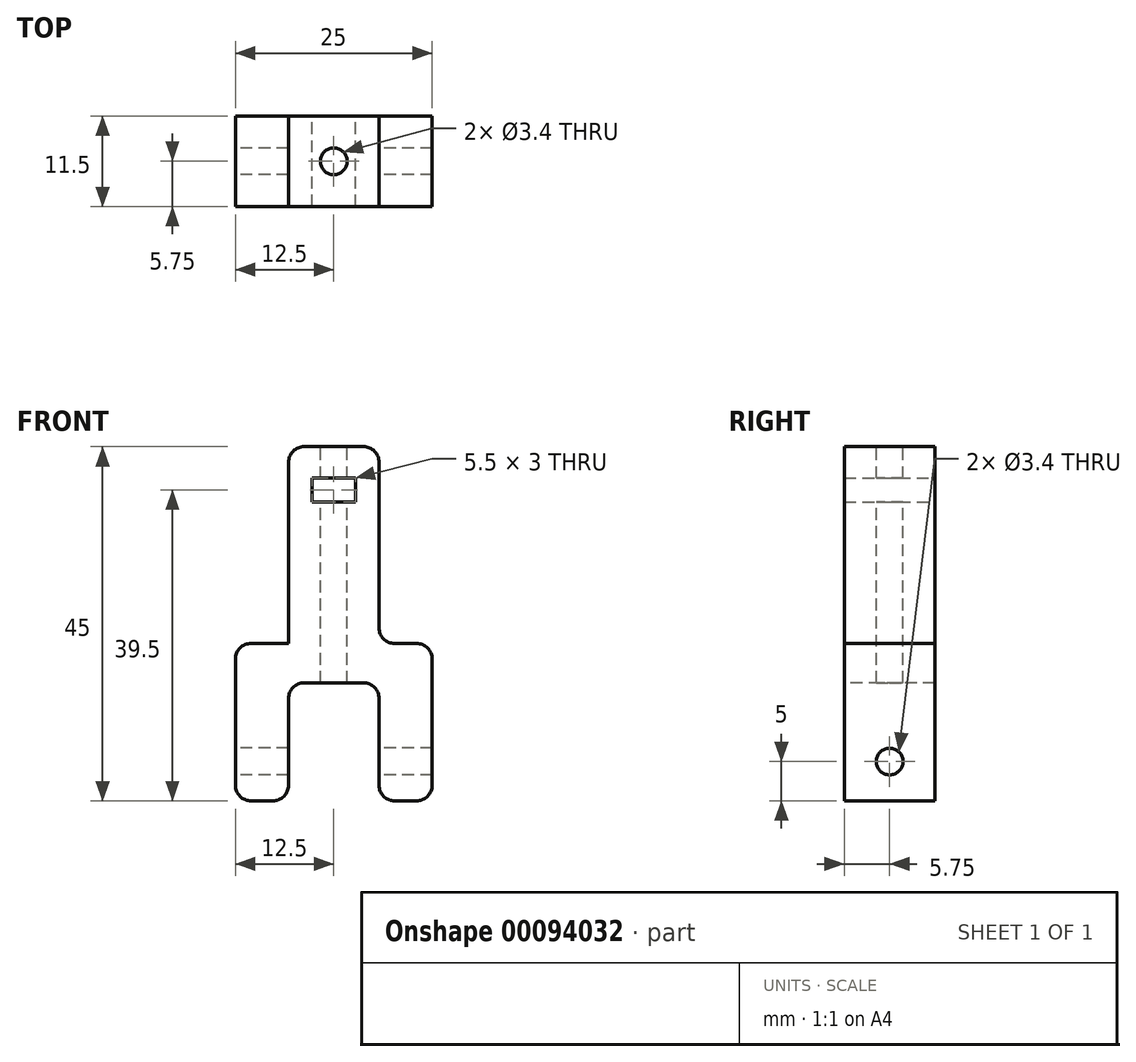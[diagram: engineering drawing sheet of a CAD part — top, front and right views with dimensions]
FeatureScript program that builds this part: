
annotation { "Feature Type Name" : "Feature", "Feature Type Description" : "" }
export const myFeature = defineFeature(function(context is Context, id is Id, definition is map)
    precondition{}
    {
        {
            var Q0;
            Q0=qCreatedBy(makeId("Top.planeOp"),FACE);
            var sketch = newSketch(context, id + "F0", { "sketchPlane" : qUnion([Q0])});
            skLineSegment(sketch, "E0.bottom", {"start": v(5.75, 5.75) * mm, "end": v(-5.75, 5.75) * mm});
            skLineSegment(sketch, "E0.top", {"start": v(5.75, -5.75) * mm, "end": v(-5.75, -5.75) * mm});
            skLineSegment(sketch, "E0.left", {"start": v(5.75, 5.75) * mm, "end": v(5.75, -5.75) * mm});
            skLineSegment(sketch, "E0.right", {"start": v(-5.75, 5.75) * mm, "end": v(-5.75, -5.75) * mm});
            skPoint(sketch, "E0.middle", {"position": v(0, 0) * mm});
            skLineSegment(sketch, "E1.bottom", {"start": v(12.5, 5.75) * mm, "end": v(-12.5, 5.75) * mm});
            skLineSegment(sketch, "E1.top", {"start": v(12.5, -5.75) * mm, "end": v(-12.5, -5.75) * mm});
            skLineSegment(sketch, "E1.left", {"start": v(12.5, 5.75) * mm, "end": v(12.5, -5.75) * mm});
            skLineSegment(sketch, "E1.right", {"start": v(-12.5, 5.75) * mm, "end": v(-12.5, -5.75) * mm});
            skSolve(sketch);
        }
        {
            var Q0;
            {var subQ0=sQuery(id+"F0.wireOp",EDGE,"E0.right");Q0=makeQuery(id+"F0.imprint","IMPRINT",FACE,{"disambiguationData":[TD([[makeQuery(id+"F0.imprint","IMPRINT",EDGE,{"derivedFrom":subQ0}),-1.0]])]});}
            var Q1;
            {var subQ0=sQuery(id+"F0.wireOp",EDGE,"E0.left");Q1=makeQuery(id+"F0.imprint","IMPRINT",FACE,{"disambiguationData":[TD([[makeQuery(id+"F0.imprint","IMPRINT",EDGE,{"derivedFrom":subQ0}),1.0]])]});}
            var Q2;
            {var subQ0=sQuery(id+"F0.wireOp",EDGE,"E0.left");Q2=makeQuery(id+"F0.imprint","IMPRINT",FACE,{"disambiguationData":[TD([[makeQuery(id+"F0.imprint","IMPRINT",EDGE,{"derivedFrom":subQ0}),-1.0]])]});}
            extrude(context, id + "F1", {"entities" : qUnion([Q0, Q1, Q2]), "oppositeDirection" : true, "depth" : 5 * mm});
        }
        {
            var Q0;
            {var subQ0=sQuery(id+"F0.wireOp",EDGE,"E0.left");Q0=makeQuery(id+"F0.imprint","IMPRINT",FACE,{"disambiguationData":[TD([[makeQuery(id+"F0.imprint","IMPRINT",EDGE,{"derivedFrom":subQ0}),1.0]])]});}
            var Q1;
            {var subQ0=sQuery(id+"F0.wireOp",EDGE,"E0.right");Q1=makeQuery(id+"F0.imprint","IMPRINT",FACE,{"disambiguationData":[TD([[makeQuery(id+"F0.imprint","IMPRINT",EDGE,{"derivedFrom":subQ0}),-1.0]])]});}
            extrude(context, id + "F2", {"entities" : qUnion([Q0, Q1]), "operationType" : NewBodyOperationType.ADD, "oppositeDirection" : true, "depth" : 20 * mm});
        }
        {
            var Q0;
            {var subQ0=sQuery(id+"F0.wireOp",EDGE,"E0.left");Q0=makeQuery(id+"F0.imprint","IMPRINT",FACE,{"disambiguationData":[TD([[makeQuery(id+"F0.imprint","IMPRINT",EDGE,{"derivedFrom":subQ0}),-1.0]])]});}
            extrude(context, id + "F3", {"entities" : qUnion([Q0]), "operationType" : NewBodyOperationType.ADD, "depth" : 25 * mm});
        }
        {
            var Q0;
            {var subQ0=sQuery(id+"F0.wireOp",EDGE,"E1.right");Q0=makeQuery(id+"F2.boolean.opBoolean","MERGE",FACE,{"derivedFrom":[makeQuery(id+"F1.opExtrude","SWEPT_FACE",FACE,{"disambiguationData":[OSD([subQ0])]}),makeQuery(id+"F2.opExtrude","SWEPT_FACE",FACE,{"disambiguationData":[OSD([subQ0])]})]});}
            var sketch = newSketch(context, id + "F4", { "sketchPlane" : qUnion([Q0])});
            skCircle(sketch, "E2", {"center": v(0, -15) * mm, "radius": 1.7 * mm});
            skSolve(sketch);
        }
        {
            var Q0;
            Q0 = qSketchRegion(id + "F4", true);
            extrude(context, id + "F5", {"entities" : qUnion([Q0]), "operationType" : NewBodyOperationType.REMOVE, "endBound" : BoundingType.THROUGH_ALL, "oppositeDirection" : true, "depth" : 25 * mm});
        }
        {
            var Q0;
            {var subQ0=sQuery(id+"F0.wireOp",EDGE,"E1.bottom");Q0=makeQuery(id+"F3.boolean.opBoolean","MERGE",FACE,{"derivedFrom":[makeQuery(id+"F2.boolean.opBoolean","MERGE",FACE,{"derivedFrom":[makeQuery(id+"F1.opExtrude","SWEPT_FACE",FACE,{"disambiguationData":[OSD([subQ0])]}),makeQuery(id+"F2.opExtrude","SWEPT_FACE",FACE,{"disambiguationData":[OSD([subQ0]),TDD([makeQuery(id+"F0.imprint","IMPRINT",EDGE,{"disambiguationData":[TD([[makeQuery(id+"F0.imprint","INTERSECT",VERTEX,{"derivedFrom":[sQuery(id+"F0.wireOp",EDGE,"E0.left"),subQ0]}),1.0]])],"derivedFrom":subQ0})])]}),makeQuery(id+"F2.opExtrude","SWEPT_FACE",FACE,{"disambiguationData":[OSD([subQ0]),TDD([makeQuery(id+"F0.imprint","IMPRINT",EDGE,{"disambiguationData":[TD([[makeQuery(id+"F0.imprint","INTERSECT",VERTEX,{"derivedFrom":[sQuery(id+"F0.wireOp",EDGE,"E0.right"),subQ0]}),-1.0]])],"derivedFrom":subQ0})])]})]}),makeQuery(id+"F3.opExtrude","SWEPT_FACE",FACE,{"disambiguationData":[OSD([subQ0])]})]});}
            var sketch = newSketch(context, id + "F6", { "sketchPlane" : qUnion([Q0])});
            skLineSegment(sketch, "E3.bottom", {"start": v(2.75, 21) * mm, "end": v(-2.75, 21) * mm});
            skLineSegment(sketch, "E3.top", {"start": v(2.75, 18) * mm, "end": v(-2.75, 18) * mm});
            skLineSegment(sketch, "E3.left", {"start": v(2.75, 21) * mm, "end": v(2.75, 18) * mm});
            skLineSegment(sketch, "E3.right", {"start": v(-2.75, 21) * mm, "end": v(-2.75, 18) * mm});
            skPoint(sketch, "E3.middle", {"position": v(0, 19.5) * mm});
            skSolve(sketch);
        }
        {
            var Q0;
            Q0=makeQuery(id+"F6.imprint","IMPRINT",FACE,{"disambiguationData":[TD([[makeQuery(id+"F6.imprint","IMPRINT",EDGE,{"derivedFrom":sQuery(id+"F6.wireOp",EDGE,"E3.bottom")}),1.0]])]});
            extrude(context, id + "F7", {"entities" : qUnion([Q0]), "operationType" : NewBodyOperationType.REMOVE, "endBound" : BoundingType.THROUGH_ALL, "oppositeDirection" : true, "depth" : 25 * mm});
        }
        {
            var Q0;
            Q0=makeQuery(id+"F3.opExtrude","CAP_FACE",FACE,{"disambiguationData":[OSD([sQuery(id+"F0.wireOp",EDGE,"E0.left"),sQuery(id+"F0.wireOp",EDGE,"E0.right"),sQuery(id+"F0.wireOp",EDGE,"E1.bottom"),sQuery(id+"F0.wireOp",EDGE,"E1.top")])],"isStart":false});
            var sketch = newSketch(context, id + "F8", { "sketchPlane" : qUnion([Q0])});
            skCircle(sketch, "E4", {"center": v(0, 0) * mm, "radius": 1.7 * mm});
            skSolve(sketch);
        }
        {
            var Q0;
            Q0 = qSketchRegion(id + "F8", true);
            extrude(context, id + "F9", {"entities" : qUnion([Q0]), "operationType" : NewBodyOperationType.REMOVE, "endBound" : BoundingType.THROUGH_ALL, "oppositeDirection" : true, "depth" : 25 * mm});
        }
        {
            var Q0;
            Q0=makeQuery(id+"F2.opExtrude","CAP_EDGE",EDGE,{"disambiguationData":[OSD([sQuery(id+"F0.wireOp",EDGE,"E0.right")])],"isStart":false});
            var Q1;
            Q1=makeQuery(id+"F2.opExtrude","CAP_EDGE",EDGE,{"disambiguationData":[OSD([sQuery(id+"F0.wireOp",EDGE,"E1.right")])],"isStart":false});
            var Q2;
            Q2=makeQuery(id+"F2.boolean.opBoolean","INTERSECT",EDGE,{"derivedFrom":[makeQuery(id+"F1.opExtrude","CAP_FACE",FACE,{"disambiguationData":[OSD([sQuery(id+"F0.wireOp",EDGE,"E1.bottom"),sQuery(id+"F0.wireOp",EDGE,"E1.top"),sQuery(id+"F0.wireOp",EDGE,"E1.left"),sQuery(id+"F0.wireOp",EDGE,"E1.right")])],"isStart":false}),makeQuery(id+"F2.opExtrude","SWEPT_FACE",FACE,{"disambiguationData":[OSD([sQuery(id+"F0.wireOp",EDGE,"E0.right")])]})]});
            var Q3;
            Q3=makeQuery(id+"F2.boolean.opBoolean","INTERSECT",EDGE,{"derivedFrom":[makeQuery(id+"F1.opExtrude","CAP_FACE",FACE,{"disambiguationData":[OSD([sQuery(id+"F0.wireOp",EDGE,"E1.bottom"),sQuery(id+"F0.wireOp",EDGE,"E1.top"),sQuery(id+"F0.wireOp",EDGE,"E1.left"),sQuery(id+"F0.wireOp",EDGE,"E1.right")])],"isStart":false}),makeQuery(id+"F2.opExtrude","SWEPT_FACE",FACE,{"disambiguationData":[OSD([sQuery(id+"F0.wireOp",EDGE,"E0.left")])]})]});
            var Q4;
            Q4=makeQuery(id+"F2.opExtrude","CAP_EDGE",EDGE,{"disambiguationData":[OSD([sQuery(id+"F0.wireOp",EDGE,"E0.left")])],"isStart":false});
            var Q5;
            Q5=makeQuery(id+"F2.opExtrude","CAP_EDGE",EDGE,{"disambiguationData":[OSD([sQuery(id+"F0.wireOp",EDGE,"E1.left")])],"isStart":false});
            var Q6;
            Q6=makeQuery(id+"F1.opExtrude","CAP_EDGE",EDGE,{"disambiguationData":[OSD([sQuery(id+"F0.wireOp",EDGE,"E1.left")])],"isStart":true});
            var Q7;
            Q7=makeQuery(id+"F1.opExtrude","CAP_EDGE",EDGE,{"disambiguationData":[OSD([sQuery(id+"F0.wireOp",EDGE,"E1.right")])],"isStart":true});
            var Q8;
            Q8=makeQuery(id+"F3.opExtrude","CAP_EDGE",EDGE,{"disambiguationData":[OSD([sQuery(id+"F0.wireOp",EDGE,"E0.right")])],"isStart":true});
            var Q9;
            Q9=makeQuery(id+"F3.opExtrude","CAP_EDGE",EDGE,{"disambiguationData":[OSD([sQuery(id+"F0.wireOp",EDGE,"E0.right")])],"isStart":false});
            var Q10;
            Q10=makeQuery(id+"F3.opExtrude","CAP_EDGE",EDGE,{"disambiguationData":[OSD([sQuery(id+"F0.wireOp",EDGE,"E0.left")])],"isStart":false});
            var Q11;
            Q11=makeQuery(id+"F3.opExtrude","CAP_EDGE",EDGE,{"disambiguationData":[OSD([sQuery(id+"F0.wireOp",EDGE,"E0.left")])],"isStart":true});
            fillet(context, id + "F10", {"entities" : qUnion([Q0, Q1, Q2, Q3, Q4, Q5, Q6, Q7, Q8, Q9, Q10, Q11]), "radius" : 2 * mm, "tangentPropagation" : true, "allowEdgeOverflow" : false});
        }
    });
